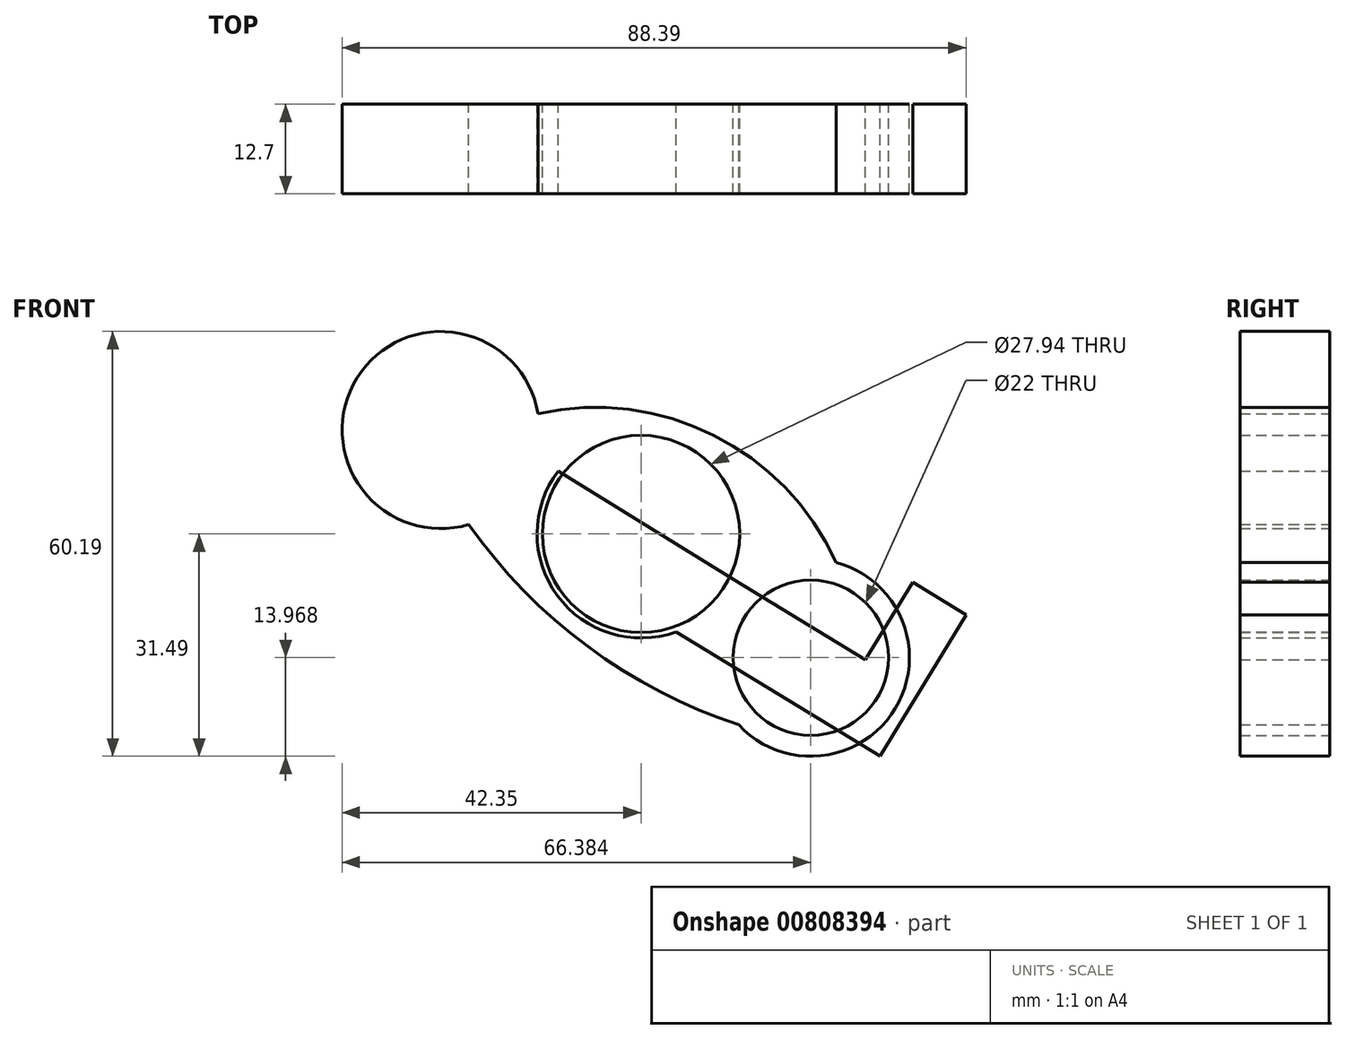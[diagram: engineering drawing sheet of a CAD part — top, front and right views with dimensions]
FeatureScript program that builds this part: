
annotation { "Feature Type Name" : "Feature", "Feature Type Description" : "" }
export const myFeature = defineFeature(function(context is Context, id is Id, definition is map)
    precondition{}
    {
        {
            var Q0;
            Q0=qCreatedBy(makeId("Front.planeOp"),FACE);
            var sketch = newSketch(context, id + "F0", { "sketchPlane" : qUnion([Q0])});
            skCircle(sketch, "E0", {"center": v(0, 0) * mm, "radius": 14.74 * mm});
            skLineSegment(sketch, "E1", {"start": v(13.21, -6.53) * mm, "end": v(31.79, -17.83) * mm});
            skLineSegment(sketch, "E2", {"start": v(31.79, -17.83) * mm, "end": v(38.48, -6.84) * mm});
            skLineSegment(sketch, "E3", {"start": v(38.48, -6.84) * mm, "end": v(46.04, -11.45) * mm});
            skLineSegment(sketch, "E4", {"start": v(46.04, -11.45) * mm, "end": v(33.86, -31.47) * mm});
            skLineSegment(sketch, "E5", {"start": v(33.86, -31.47) * mm, "end": v(4.95, -13.88) * mm});
            skLineSegment(sketch, "E6", {"start": v(4.95, -13.88) * mm, "end": v(-38.85, 12.78) * mm});
            skLineSegment(sketch, "E7", {"start": v(13.21, -6.53) * mm, "end": v(-32.72, 21.86) * mm});
            skLineSegment(sketch, "E8", {"start": v(-32.72, 21.86) * mm, "end": v(-38.85, 12.78) * mm});
            skSolve(sketch);
        }
        {
            var Q0;
            Q0=qCreatedBy(makeId("Front.planeOp"),FACE);
            var sketch = newSketch(context, id + "F1", { "sketchPlane" : qUnion([Q0])});
            skCircle(sketch, "E9", {"center": v(-28.38, 14.73) * mm, "radius": 11 * mm});
            skCircle(sketch, "E10", {"center": v(24.03, -17.52) * mm, "radius": 11 * mm});
            skCircle(sketch, "E11", {"center": v(-28.38, 14.73) * mm, "radius": 13.97 * mm});
            skCircle(sketch, "E12", {"center": v(24.03, -17.52) * mm, "radius": 13.97 * mm});
            skCircle(sketch, "E13", {"center": v(0, 0) * mm, "radius": 13.97 * mm});
            skArc(sketch, "E14", {"start": v(-24.42, 1.33) * mm, "mid": v(-7.57, -15.93) * mm, "end": v(13.82, -27.06) * mm});
            skArc(sketch, "E15", {"start": v(27.61, -4.02) * mm, "mid": v(10.25, 14) * mm, "end": v(-14.6, 17.04) * mm});
            skSolve(sketch);
        }
        {
            var Q0;
            {var subQ0=sQuery(id+"F0.wireOp",EDGE,"E6");var subQ1=sQuery(id+"F0.wireOp",EDGE,"E0");var subQ3=makeQuery(id+"F0.imprint","INTERSECT",VERTEX,{"derivedFrom":[subQ1,subQ0]});Q0=makeQuery(id+"F0.imprint","IMPRINT",FACE,{"disambiguationData":[TD([[makeQuery(id+"F0.imprint","IMPRINT",EDGE,{"disambiguationData":[TD([[subQ3,-1.0]])],"derivedFrom":subQ1}),1.0]])]});}
            var Q1;
            Q1=makeQuery(id+"F1.imprint","IMPRINT",FACE,{"disambiguationData":[TD([[makeQuery(id+"F1.imprint","IMPRINT",EDGE,{"derivedFrom":sQuery(id+"F1.wireOp",EDGE,"E13")}),-1.0]])]});
            var Q2;
            Q2=makeQuery(id+"F1.imprint","IMPRINT",FACE,{"disambiguationData":[TD([[makeQuery(id+"F1.imprint","IMPRINT",EDGE,{"derivedFrom":sQuery(id+"F1.wireOp",EDGE,"E10")}),-1.0]])]});
            var Q3;
            {var subQ0=sQuery(id+"F0.wireOp",EDGE,"E1");Q3=makeQuery(id+"F0.imprint","IMPRINT",FACE,{"disambiguationData":[TD([[makeQuery(id+"F0.imprint","IMPRINT",EDGE,{"derivedFrom":subQ0}),-1.0]])]});}
            var Q4;
            {var subQ0=sQuery(id+"F0.wireOp",EDGE,"E6");var subQ1=sQuery(id+"F0.wireOp",EDGE,"E0");var subQ2=makeQuery(id+"F0.imprint","INTERSECT",VERTEX,{"derivedFrom":[subQ1,subQ0]});Q4=makeQuery(id+"F0.imprint","IMPRINT",FACE,{"disambiguationData":[TD([[makeQuery(id+"F0.imprint","IMPRINT",EDGE,{"disambiguationData":[TD([[subQ2,1.0]])],"derivedFrom":subQ1}),1.0]])]});}
            var Q5;
            Q5=makeQuery(id+"F1.imprint","IMPRINT",FACE,{"disambiguationData":[TD([[makeQuery(id+"F1.imprint","IMPRINT",EDGE,{"derivedFrom":sQuery(id+"F1.wireOp",EDGE,"E9")}),1.0]])]});
            var Q6;
            Q6=makeQuery(id+"F1.imprint","IMPRINT",FACE,{"disambiguationData":[TD([[makeQuery(id+"F1.imprint","IMPRINT",EDGE,{"derivedFrom":sQuery(id+"F1.wireOp",EDGE,"E9")}),-1.0]])]});
            extrude(context, id + "F2", {"entities" : qUnion([Q0, Q1, Q2, Q3, Q4, Q5, Q6]), "depth" : 12.7 * mm, "offsetDistance" : 25.4 * mm});
        }
    });
